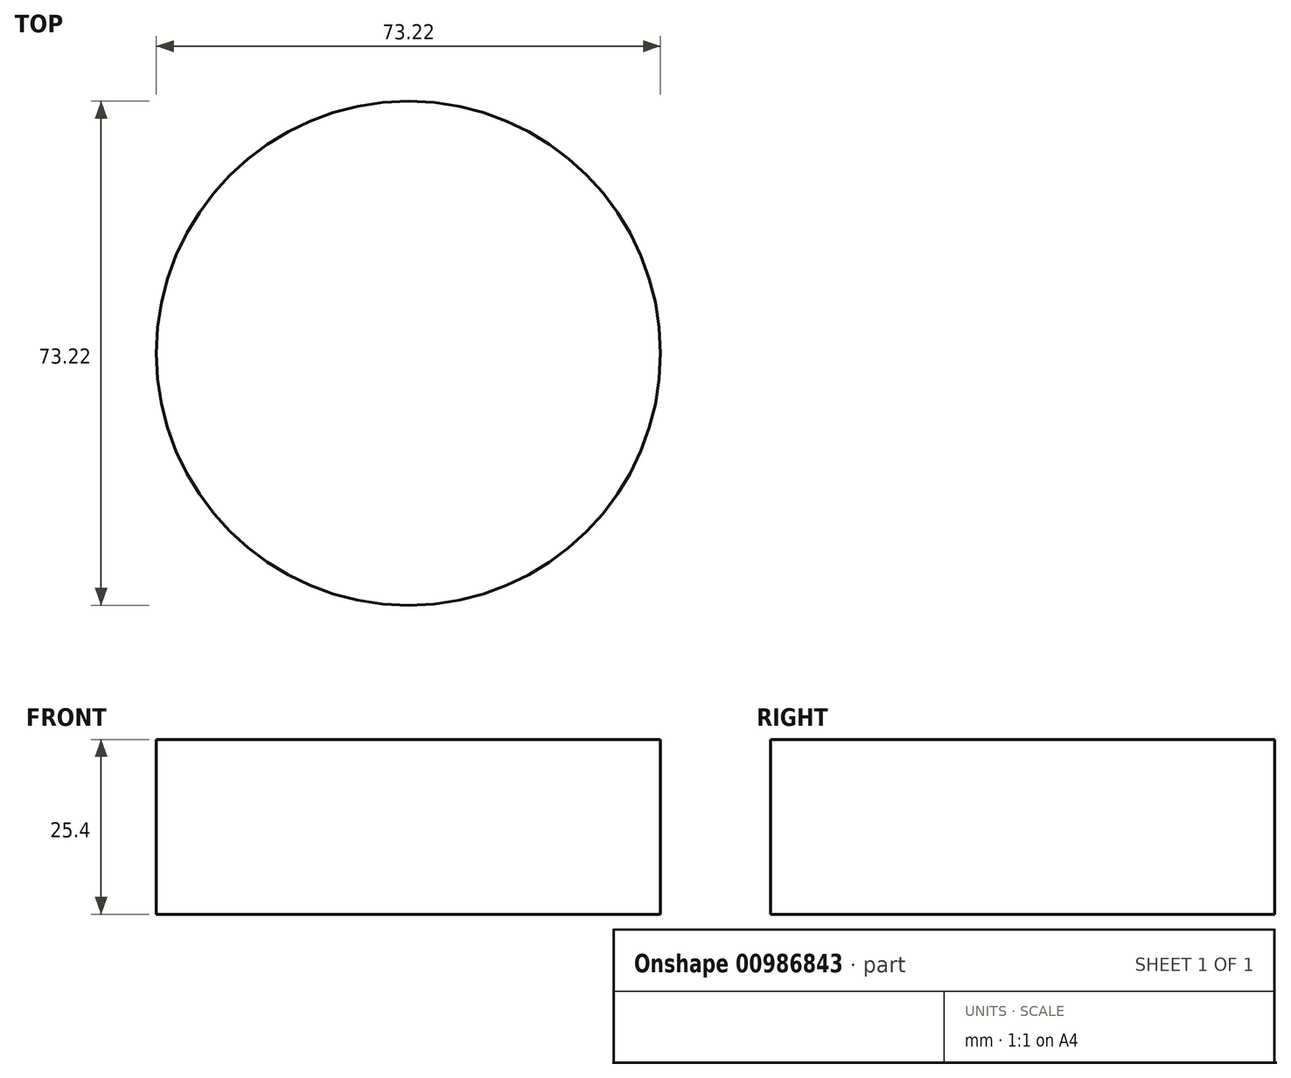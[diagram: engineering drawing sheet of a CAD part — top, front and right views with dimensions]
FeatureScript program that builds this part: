
annotation { "Feature Type Name" : "Feature", "Feature Type Description" : "" }
export const myFeature = defineFeature(function(context is Context, id is Id, definition is map)
    precondition{}
    {
        {
            var Q0;
            Q0=qCreatedBy(makeId("Top.planeOp"),FACE);
            var sketch = newSketch(context, id + "F0", { "sketchPlane" : qUnion([Q0])});
            skCircle(sketch, "E0", {"center": v(0, 0) * mm, "radius": 36.61 * mm});
            skSolve(sketch);
        }
        {
            var Q0;
            Q0=makeQuery(id+"F0.imprint","IMPRINT",FACE,{"disambiguationData":[TD([[makeQuery(id+"F0.imprint","IMPRINT",EDGE,{"derivedFrom":sQuery(id+"F0.wireOp",EDGE,"E0")}),1.0]])]});
            extrude(context, id + "F1", {"entities" : qUnion([Q0]), "depth" : 25.4 * mm, "offsetDistance" : 25.4 * mm});
        }
    });
